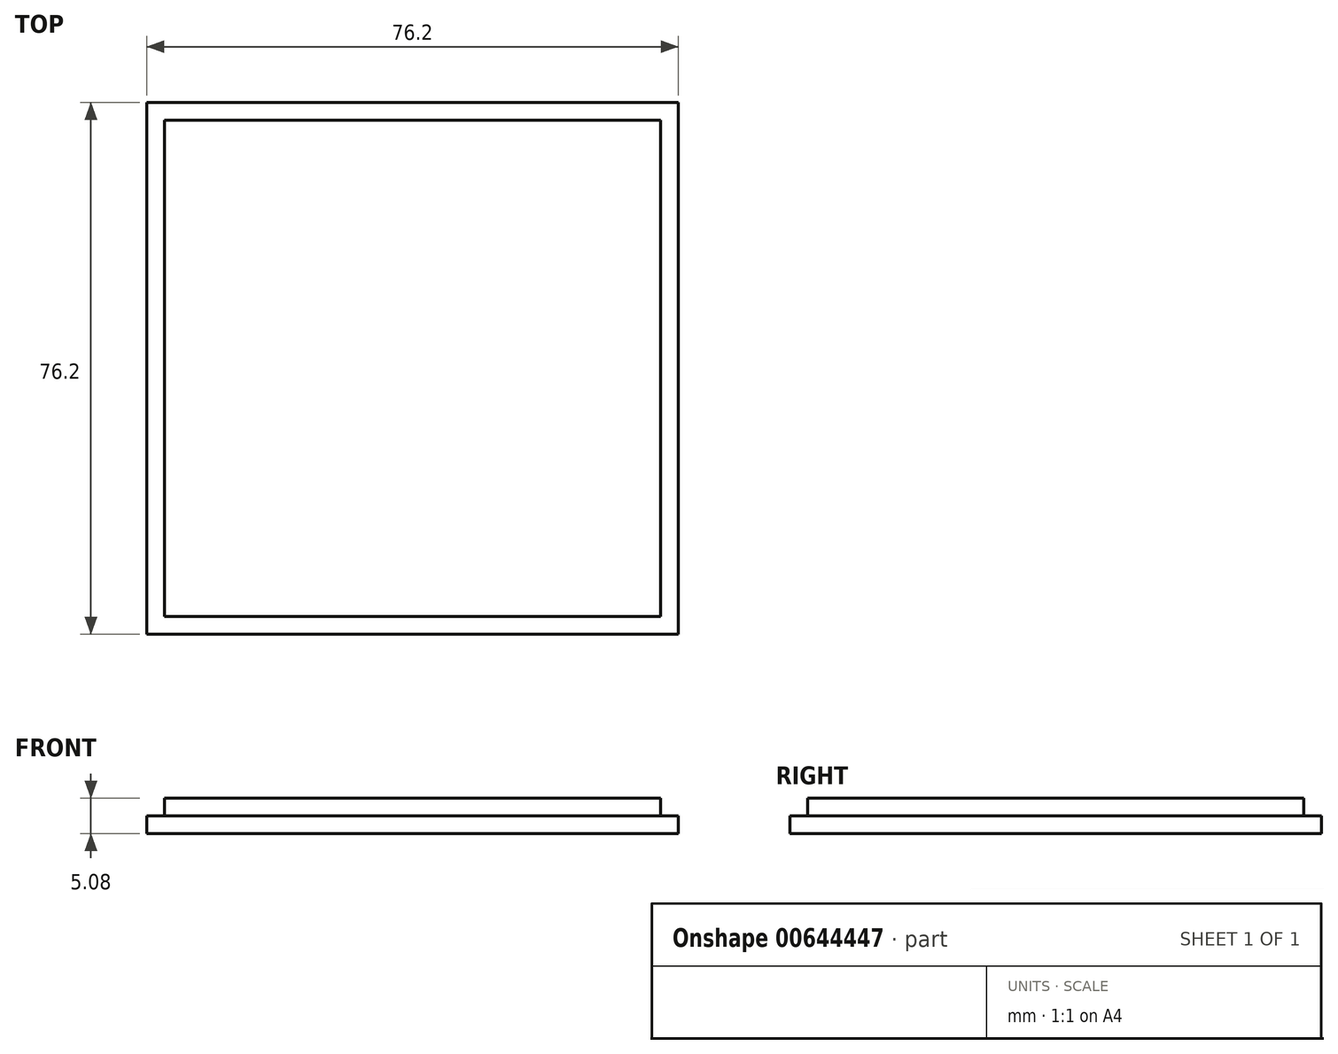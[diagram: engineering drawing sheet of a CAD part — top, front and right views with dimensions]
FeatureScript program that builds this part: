
annotation { "Feature Type Name" : "Feature", "Feature Type Description" : "" }
export const myFeature = defineFeature(function(context is Context, id is Id, definition is map)
    precondition{}
    {
        {
            var Q0;
            Q0=qCreatedBy(makeId("Top.planeOp"),FACE);
            var sketch = newSketch(context, id + "F0", { "sketchPlane" : qUnion([Q0])});
            skLineSegment(sketch, "E0.bottom", {"start": v(38.1, 38.1) * mm, "end": v(-38.1, 38.1) * mm});
            skLineSegment(sketch, "E0.top", {"start": v(38.1, -38.1) * mm, "end": v(-38.1, -38.1) * mm});
            skLineSegment(sketch, "E0.left", {"start": v(38.1, 38.1) * mm, "end": v(38.1, -38.1) * mm});
            skLineSegment(sketch, "E0.right", {"start": v(-38.1, 38.1) * mm, "end": v(-38.1, -38.1) * mm});
            skPoint(sketch, "E0.middle", {"position": v(0, 0) * mm});
            skSolve(sketch);
        }
        {
            var Q0;
            Q0 = qSketchRegion(id + "F0", true);
            extrude(context, id + "F1", {"entities" : qUnion([Q0]), "depth" : 2.54 * mm, "offsetDistance" : 25.4 * mm});
        }
        {
            var Q0;
            Q0=makeQuery(id+"F1.opExtrude","CAP_FACE",FACE,{"disambiguationData":[OSD([sQuery(id+"F0.wireOp",EDGE,"E0.bottom"),sQuery(id+"F0.wireOp",EDGE,"E0.top"),sQuery(id+"F0.wireOp",EDGE,"E0.left"),sQuery(id+"F0.wireOp",EDGE,"E0.right")])],"isStart":false});
            var sketch = newSketch(context, id + "F2", { "sketchPlane" : qUnion([Q0])});
            skLineSegment(sketch, "E1.0", {"start": v(35.56, 35.56) * mm, "end": v(-35.56, 35.56) * mm});
            skLineSegment(sketch, "E1.1", {"start": v(35.56, 35.56) * mm, "end": v(35.56, -35.56) * mm});
            skLineSegment(sketch, "E1.2", {"start": v(35.56, -35.56) * mm, "end": v(-35.56, -35.56) * mm});
            skLineSegment(sketch, "E1.3", {"start": v(-35.56, 35.56) * mm, "end": v(-35.56, -35.56) * mm});
            skSolve(sketch);
        }
        {
            var Q0;
            Q0 = qSketchRegion(id + "F2", true);
            extrude(context, id + "F3", {"entities" : qUnion([Q0]), "operationType" : NewBodyOperationType.ADD, "depth" : 2.54 * mm, "offsetDistance" : 25.4 * mm});
        }
    });
